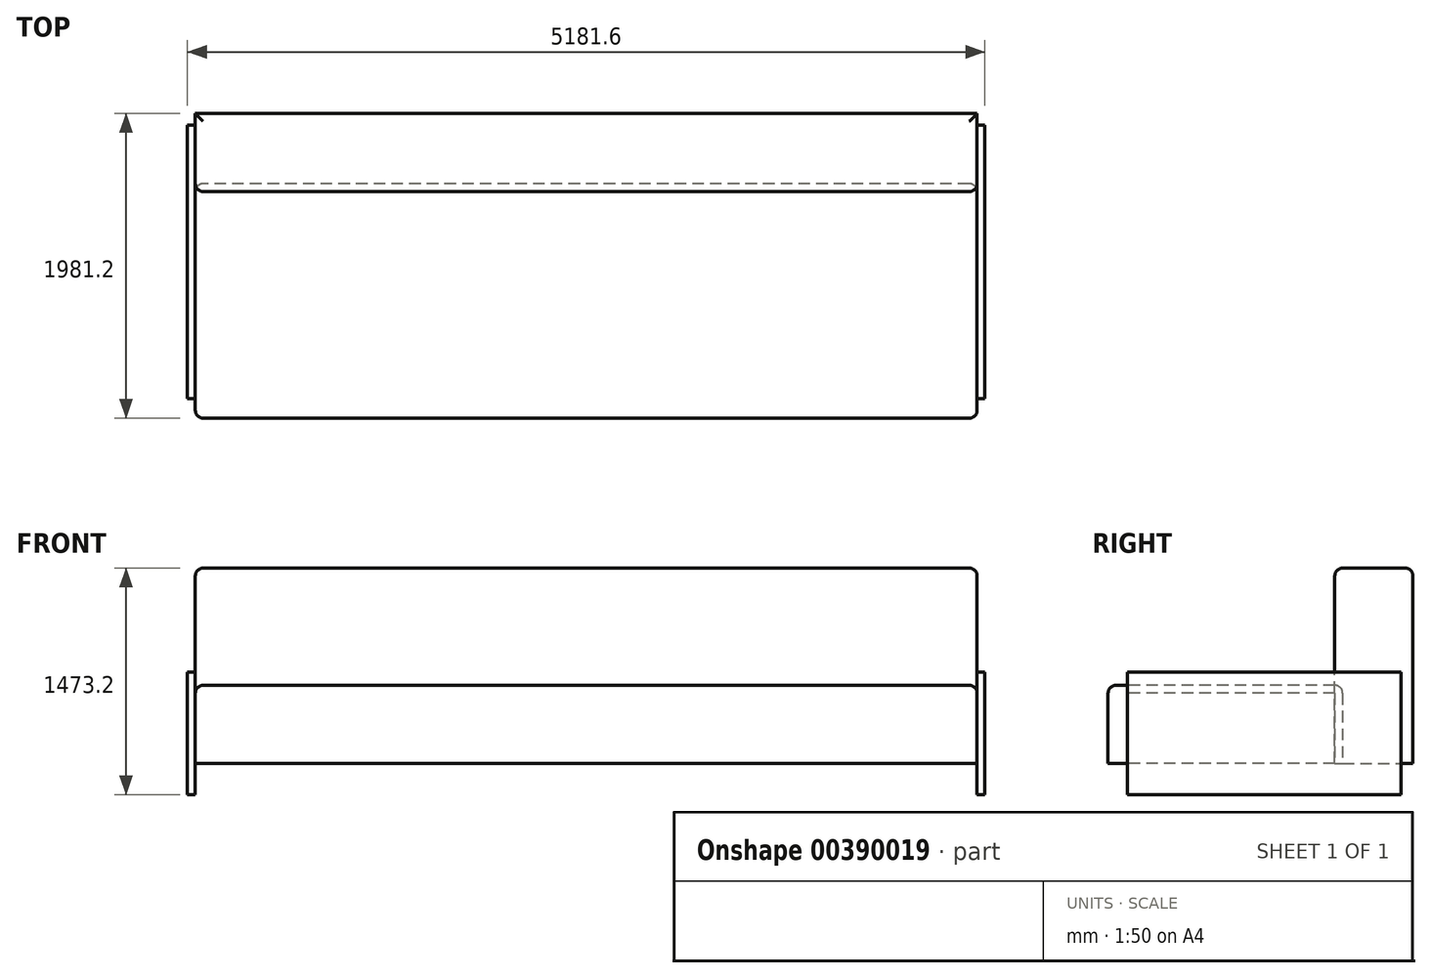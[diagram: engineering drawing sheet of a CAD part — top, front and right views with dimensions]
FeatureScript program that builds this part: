
annotation { "Feature Type Name" : "Feature", "Feature Type Description" : "" }
export const myFeature = defineFeature(function(context is Context, id is Id, definition is map)
    precondition{}
    {
        {
            var Q0;
            Q0=qCreatedBy(makeId("Top.planeOp"),FACE);
            var sketch = newSketch(context, id + "F0", { "sketchPlane" : qUnion([Q0])});
            skLineSegment(sketch, "E0.bottom", {"start": v(2540, 762) * mm, "end": v(-2540, 762) * mm});
            skLineSegment(sketch, "E0.top", {"start": v(2540, -762) * mm, "end": v(-2540, -762) * mm});
            skLineSegment(sketch, "E0.left", {"start": v(2540, 762) * mm, "end": v(2540, -762) * mm});
            skLineSegment(sketch, "E0.right", {"start": v(-2540, 762) * mm, "end": v(-2540, -762) * mm});
            skPoint(sketch, "E0.middle", {"position": v(0, 0) * mm});
            skSolve(sketch);
        }
        {
            var Q0;
            Q0 = qSketchRegion(id + "F0", true);
            extrude(context, id + "F1", {"entities" : qUnion([Q0]), "depth" : 508 * mm});
        }
        {
            var Q0;
            Q0=makeQuery(id+"F1.opExtrude","SWEPT_EDGE",EDGE,{"disambiguationData":[OSD([sQuery(id+"F0.wireOp",EDGE,"E0.bottom"),sQuery(id+"F0.wireOp",EDGE,"E0.right")])]});
            var Q1;
            Q1=makeQuery(id+"F1.opExtrude","SWEPT_EDGE",EDGE,{"disambiguationData":[OSD([sQuery(id+"F0.wireOp",EDGE,"E0.top"),sQuery(id+"F0.wireOp",EDGE,"E0.right")])]});
            var Q2;
            Q2=makeQuery(id+"F1.opExtrude","SWEPT_EDGE",EDGE,{"disambiguationData":[OSD([sQuery(id+"F0.wireOp",EDGE,"E0.top"),sQuery(id+"F0.wireOp",EDGE,"E0.left")])]});
            var Q3;
            Q3=makeQuery(id+"F1.opExtrude","SWEPT_EDGE",EDGE,{"disambiguationData":[OSD([sQuery(id+"F0.wireOp",EDGE,"E0.bottom"),sQuery(id+"F0.wireOp",EDGE,"E0.left")])]});
            var Q4;
            Q4=makeQuery(id+"F1.opExtrude","CAP_EDGE",EDGE,{"disambiguationData":[OSD([sQuery(id+"F0.wireOp",EDGE,"E0.left")])],"isStart":false});
            var Q5;
            Q5=makeQuery(id+"F1.opExtrude","CAP_EDGE",EDGE,{"disambiguationData":[OSD([sQuery(id+"F0.wireOp",EDGE,"E0.top")])],"isStart":false});
            var Q6;
            Q6=makeQuery(id+"F1.opExtrude","CAP_EDGE",EDGE,{"disambiguationData":[OSD([sQuery(id+"F0.wireOp",EDGE,"E0.bottom")])],"isStart":false});
            var Q7;
            Q7=makeQuery(id+"F1.opExtrude","CAP_EDGE",EDGE,{"disambiguationData":[OSD([sQuery(id+"F0.wireOp",EDGE,"E0.right")])],"isStart":false});
            fillet(context, id + "F2", {"entities" : qUnion([Q0, Q1, Q2, Q3, Q4, Q5, Q6, Q7]), "radius" : 50.8 * mm, "tangentPropagation" : true, "allowEdgeOverflow" : false});
        }
        {
            var Q0;
            Q0=makeQuery(id+"F1.opExtrude","SWEPT_FACE",FACE,{"disambiguationData":[OSD([sQuery(id+"F0.wireOp",EDGE,"E0.right")])]});
            var sketch = newSketch(context, id + "F3", { "sketchPlane" : qUnion([Q0])});
            skLineSegment(sketch, "E1.bottom", {"start": v(-1143, 595.52) * mm, "end": v(635, 595.52) * mm});
            skLineSegment(sketch, "E1.top", {"start": v(-1143, -203.2) * mm, "end": v(635, -203.2) * mm});
            skLineSegment(sketch, "E1.left", {"start": v(-1143, 595.52) * mm, "end": v(-1143, -203.2) * mm});
            skLineSegment(sketch, "E1.right", {"start": v(635, 595.52) * mm, "end": v(635, -203.2) * mm});
            skSolve(sketch);
        }
        {
            var Q0;
            Q0 = qSketchRegion(id + "F3", true);
            extrude(context, id + "F4", {"entities" : qUnion([Q0]), "depth" : 50.8 * mm});
        }
        {
            var Q0;
            Q0=makeQuery(id+"F4.opExtrude","SWEPT_BODY",BODY,{"disambiguationData":[OSD([sQuery(id+"F3.wireOp",EDGE,"E1.bottom"),sQuery(id+"F3.wireOp",EDGE,"E1.top"),sQuery(id+"F3.wireOp",EDGE,"E1.left"),sQuery(id+"F3.wireOp",EDGE,"E1.right")])]});
            var Q1;
            Q1=qCreatedBy(makeId("Right.planeOp"),FACE);
            mirror(context, id + "F5", {"operationType" : NewBodyOperationType.ADD, "entities" : qUnion([Q0]), "mirrorPlane" : qUnion([Q1])});
        }
        {
            var Q0;
            Q0=makeQuery(id+"F4.opExtrude","CAP_FACE",FACE,{"disambiguationData":[OSD([sQuery(id+"F3.wireOp",EDGE,"E1.bottom"),sQuery(id+"F3.wireOp",EDGE,"E1.top"),sQuery(id+"F3.wireOp",EDGE,"E1.left"),sQuery(id+"F3.wireOp",EDGE,"E1.right")])],"isStart":true});
            var sketch = newSketch(context, id + "F6", { "sketchPlane" : qUnion([Q0])});
            skLineSegment(sketch, "E2.bottom", {"start": v(711.2, 0) * mm, "end": v(1219.2, 0) * mm});
            skLineSegment(sketch, "E2.top", {"start": v(711.2, 1270) * mm, "end": v(1219.2, 1270) * mm});
            skLineSegment(sketch, "E2.left", {"start": v(711.2, 0) * mm, "end": v(711.2, 1270) * mm});
            skLineSegment(sketch, "E2.right", {"start": v(1219.2, 0) * mm, "end": v(1219.2, 1270) * mm});
            skSolve(sketch);
        }
        {
            var Q0;
            Q0 = qSketchRegion(id + "F6", true);
            extrude(context, id + "F7", {"entities" : qUnion([Q0]), "depth" : 5080 * mm});
        }
        {
            var Q0;
            Q0=makeQuery(id+"F7.opExtrude","SWEPT_EDGE",EDGE,{"disambiguationData":[OSD([sQuery(id+"F6.wireOp",EDGE,"E2.top"),sQuery(id+"F6.wireOp",EDGE,"E2.left")])]});
            var Q1;
            Q1=makeQuery(id+"F7.opExtrude","SWEPT_EDGE",EDGE,{"disambiguationData":[OSD([sQuery(id+"F6.wireOp",EDGE,"E2.top"),sQuery(id+"F6.wireOp",EDGE,"E2.right")])]});
            var Q2;
            Q2=makeQuery(id+"F7.opExtrude","CAP_EDGE",EDGE,{"disambiguationData":[OSD([sQuery(id+"F6.wireOp",EDGE,"E2.top")])],"isStart":false});
            var Q3;
            Q3=makeQuery(id+"F7.opExtrude","CAP_EDGE",EDGE,{"disambiguationData":[OSD([sQuery(id+"F6.wireOp",EDGE,"E2.top")])],"isStart":true});
            var Q4;
            Q4=makeQuery(id+"F7.opExtrude","CAP_EDGE",EDGE,{"disambiguationData":[OSD([sQuery(id+"F6.wireOp",EDGE,"E2.left")])],"isStart":true});
            var Q5;
            Q5=makeQuery(id+"F7.opExtrude","CAP_EDGE",EDGE,{"disambiguationData":[OSD([sQuery(id+"F6.wireOp",EDGE,"E2.left")])],"isStart":false});
            fillet(context, id + "F8", {"entities" : qUnion([Q0, Q1, Q2, Q3, Q4, Q5]), "radius" : 50.8 * mm, "tangentPropagation" : true, "allowEdgeOverflow" : false});
        }
    });
